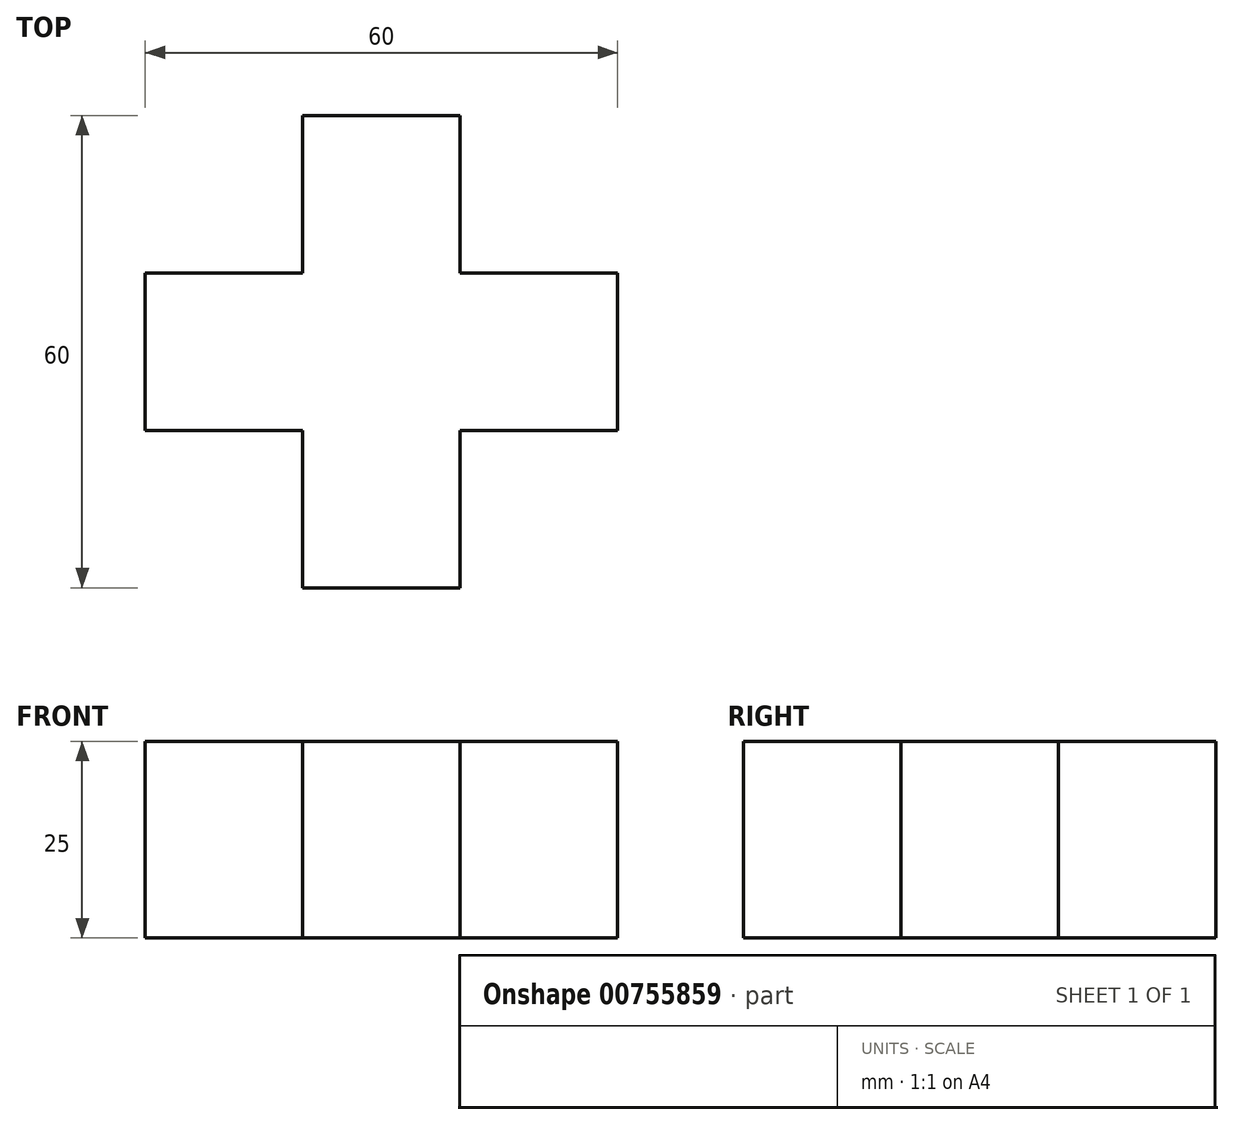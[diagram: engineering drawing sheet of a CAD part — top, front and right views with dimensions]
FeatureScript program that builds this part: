
annotation { "Feature Type Name" : "Feature", "Feature Type Description" : "" }
export const myFeature = defineFeature(function(context is Context, id is Id, definition is map)
    precondition{}
    {
        {
            var Q0;
            Q0=qCreatedBy(makeId("Top.planeOp"),FACE);
            var sketch = newSketch(context, id + "F0", { "sketchPlane" : qUnion([Q0])});
            skLineSegment(sketch, "E0.bottom", {"start": v(0, 0) * mm, "end": v(20, 0) * mm});
            skLineSegment(sketch, "E0.top", {"start": v(0, 60) * mm, "end": v(20, 60) * mm});
            skLineSegment(sketch, "E0.left", {"start": v(0, 0) * mm, "end": v(0, 60) * mm});
            skLineSegment(sketch, "E0.right", {"start": v(20, 0) * mm, "end": v(20, 60) * mm});
            skLineSegment(sketch, "E1", {"start": v(0, 30) * mm, "end": v(0, 40) * mm});
            skLineSegment(sketch, "E2", {"start": v(0, 40) * mm, "end": v(-20, 40) * mm});
            skLineSegment(sketch, "E3.bottom", {"start": v(-20, 40) * mm, "end": v(40, 40) * mm});
            skLineSegment(sketch, "E3.top", {"start": v(-20, 20) * mm, "end": v(40, 20) * mm});
            skLineSegment(sketch, "E3.left", {"start": v(-20, 40) * mm, "end": v(-20, 20) * mm});
            skLineSegment(sketch, "E3.right", {"start": v(40, 40) * mm, "end": v(40, 20) * mm});
            skSolve(sketch);
        }
        {
            var Q0;
            {var subQ0=sQuery(id+"F0.wireOp",EDGE,"E0.top");Q0=makeQuery(id+"F0.imprint","IMPRINT",FACE,{"disambiguationData":[TD([[makeQuery(id+"F0.imprint","IMPRINT",EDGE,{"derivedFrom":subQ0}),-1.0]])]});}
            var Q1;
            {var subQ1=sQuery(id+"F0.wireOp",EDGE,"E0.left");var subQ7=makeQuery(id+"F0.imprint","IMPRINT",VERTEX,{"derivedFrom":subQ1});Q1=makeQuery(id+"F0.imprint","IMPRINT",FACE,{"disambiguationData":[TD([[makeQuery(id+"F0.imprint","IMPRINT",EDGE,{"disambiguationData":[TD([[subQ7,1.0]])],"derivedFrom":subQ1}),-1.0]])]});}
            var Q2;
            {var subQ0=sQuery(id+"F0.wireOp",EDGE,"E0.bottom");Q2=makeQuery(id+"F0.imprint","IMPRINT",FACE,{"disambiguationData":[TD([[makeQuery(id+"F0.imprint","IMPRINT",EDGE,{"derivedFrom":subQ0}),1.0]])]});}
            var Q3;
            {var subQ5=sQuery(id+"F0.wireOp",EDGE,"E3.right");Q3=makeQuery(id+"F0.imprint","IMPRINT",FACE,{"disambiguationData":[TD([[makeQuery(id+"F0.imprint","IMPRINT",EDGE,{"derivedFrom":subQ5}),-1.0]])]});}
            var Q4;
            {var subQ5=sQuery(id+"F0.wireOp",EDGE,"E2");Q4=makeQuery(id+"F0.imprint","IMPRINT",FACE,{"disambiguationData":[TD([[makeQuery(id+"F0.imprint","IMPRINT",EDGE,{"derivedFrom":subQ5}),1.0]])]});}
            extrude(context, id + "F1", {"entities" : qUnion([Q0, Q1, Q2, Q3, Q4]), "depth" : 25 * mm, "offsetDistance" : 25 * mm});
        }
    });
